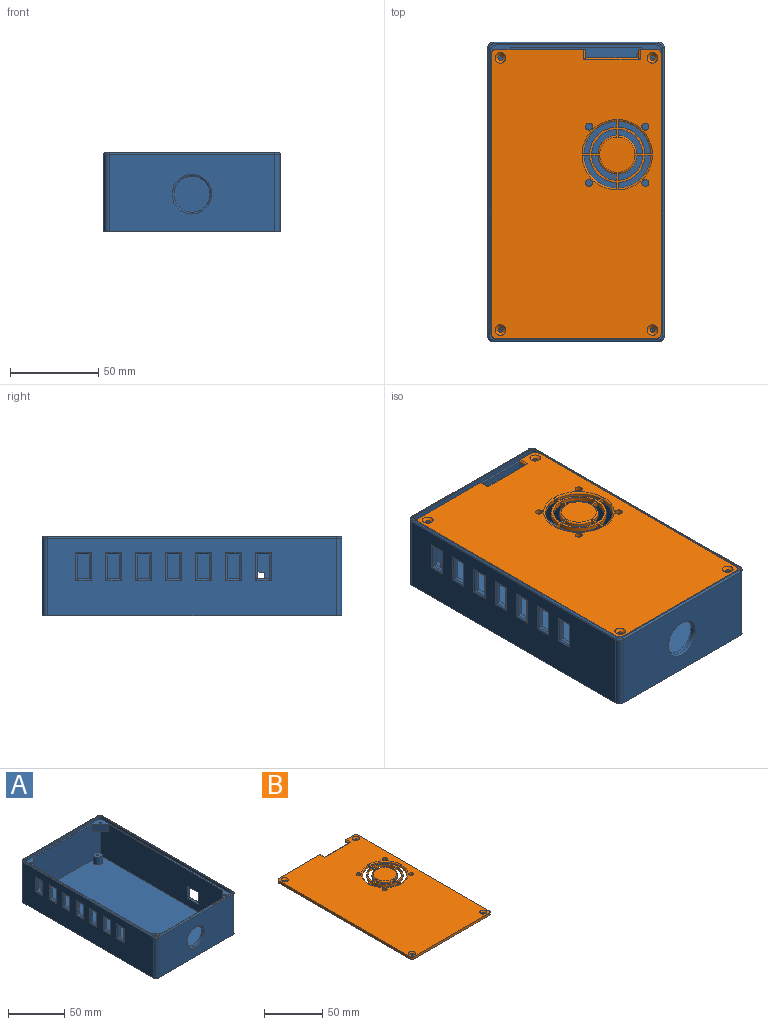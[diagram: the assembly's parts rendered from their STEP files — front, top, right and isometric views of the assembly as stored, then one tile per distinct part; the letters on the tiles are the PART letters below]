
ASSEMBLY  parts=2 mates=1
PART A: 130 faces, bbox 100.5x170.5x45 mm
  f0: plane 164x39mm, normal (-1,0,0), area 6067mm2, adj f1,f13,f14,f15,f32,f33,f34,f35
  f1: plane 94x39mm, normal (0,-1,0), area 3506mm2, adj f0,f3,f13,f14,f73,f74,f75,f76
  f2: plane 164x44mm, normal (-1,0,0), area 6208mm2, adj f8,f67,f68,f95,f98,f99,f100,f101
  f3: plane 164x39mm, normal (1,0,0), area 5550mm2, adj f1,f13,f14,f15,f36,f37,f38,f39
  f4: plane 168x98mm, normal (0,0,1), area 322.1mm2, adj f9,f10,f11,f12,f69,f70,f71,f72
  f5: plane 94x44mm, normal (0,-1,0), area 3738.4mm2, adj f8,f65,f68,f91,f97
  f6: plane 164x44mm, normal (1,0,0), area 6991mm2, adj f8,f65,f66,f90,f126,f127,f128,f129
  f7: plane 94x44mm, normal (0,1,0), area 4136mm2, adj f8,f66,f67,f94
  f8: plane 170x100mm, normal (0,0,-1), area 16992.3mm2, adj f2,f5,f6,f7,f65,f66,f67,f68
  f9: plane 90.8x3mm, normal (0,-1,0), area 272.4mm2, adj f4,f13,f69,f72
  f10: plane 160.8x3mm, normal (1,0,0), area 482.4mm2, adj f4,f13,f69,f70
  f11: plane 90.8x3mm, normal (0,1,0), area 272.4mm2, adj f4,f13,f70,f71
  f12: plane 160.8x3mm, normal (-1,0,0), area 482.4mm2, adj f4,f13,f71,f72
  f13: plane 166.8x96.8mm, normal (0,0,1), area 909.9mm2, adj f0,f1,f3,f9,f10,f11,f12,f15
  f14: plane 164x94mm, normal (0,0,1), area 15214.9mm2, adj f0,f1,f3,f15,f17,f21,f25,f29
  f15: plane 94x39mm, normal (0,1,0), area 3175.9mm2, adj f0,f3,f13,f14,f64,f77,f78,f79
  f16: cylinder r=1mm len=8mm, axis (0,0,-1), area 50.3mm2, adj f18,f19
  f17: cylinder r=4mm len=8mm, axis (0,0,-1), area 201.1mm2, adj f14,f18
  f18: plane 8x8mm, normal (0,0,1), area 47.1mm2, adj f16,f17
  f19: plane 2x2mm, normal (0,0,1), area 3.1mm2, adj f16
  f20: cylinder r=1mm len=8mm, axis (0,0,-1), area 50.3mm2, adj f22,f23
  f21: cylinder r=4mm len=8mm, axis (0,0,-1), area 201.1mm2, adj f14,f22
  f22: plane 8x8mm, normal (0,0,1), area 47.1mm2, adj f20,f21
  f23: plane 2x2mm, normal (0,0,1), area 3.1mm2, adj f20
  f24: cylinder r=1mm len=8mm, axis (0,0,-1), area 50.3mm2, adj f26,f27
  f25: cylinder r=4mm len=8mm, axis (0,0,-1), area 201.1mm2, adj f14,f26
  f26: plane 8x8mm, normal (0,0,1), area 47.1mm2, adj f24,f25
  f27: plane 2x2mm, normal (0,0,1), area 3.1mm2, adj f24
  f28: cylinder r=1mm len=8mm, axis (0,0,-1), area 50.3mm2, adj f30,f31
  f29: cylinder r=4mm len=8mm, axis (0,0,-1), area 201.1mm2, adj f14,f30
  f30: plane 8x8mm, normal (0,0,1), area 47.1mm2, adj f28,f29
  f31: plane 2x2mm, normal (0,0,1), area 3.1mm2, adj f28
  f32: plane 13x2mm, normal (0,1,0), area 26mm2, adj f0,f33,f34,f127
  f33: plane 13x2mm, normal (0,0,-1), area 26mm2, adj f0,f32,f35,f126
  f34: plane 13x2mm, normal (0,0,1), area 26mm2, adj f0,f32,f35,f129
  f35: plane 13x2mm, normal (0,-1,0), area 26mm2, adj f0,f33,f34,f128
  f36: plane 7x2mm, normal (0,0,1), area 14mm2, adj f3,f37,f39,f123
  f37: plane 14x2mm, normal (0,1,0), area 28mm2, adj f3,f36,f38,f125
  f38: plane 7x2mm, normal (0,0,-1), area 14mm2, adj f3,f37,f39,f124
  f39: plane 14x2mm, normal (0,-1,0), area 28mm2, adj f3,f36,f38,f122
  f40: plane 7x2mm, normal (0,0,1), area 14mm2, adj f3,f41,f43,f118
  f41: plane 14x2mm, normal (0,1,0), area 28mm2, adj f3,f40,f42,f119
  f42: plane 7x2mm, normal (0,0,-1), area 14mm2, adj f3,f41,f43,f121
  f43: plane 14x2mm, normal (0,-1,0), area 28mm2, adj f3,f40,f42,f120
  f44: plane 7x2mm, normal (0,0,1), area 14mm2, adj f3,f45,f47,f115
  f45: plane 14x2mm, normal (0,1,0), area 28mm2, adj f3,f44,f46,f117
  f46: plane 7x2mm, normal (0,0,-1), area 14mm2, adj f3,f45,f47,f116
  f47: plane 14x2mm, normal (0,-1,0), area 28mm2, adj f3,f44,f46,f114
  f48: plane 7x2mm, normal (0,0,1), area 14mm2, adj f3,f49,f51,f111
  f49: plane 14x2mm, normal (0,1,0), area 28mm2, adj f3,f48,f50,f113
  f50: plane 7x2mm, normal (0,0,-1), area 14mm2, adj f3,f49,f51,f112
  f51: plane 14x2mm, normal (0,-1,0), area 28mm2, adj f3,f48,f50,f110
  f52: plane 7x2mm, normal (0,0,1), area 14mm2, adj f3,f53,f55,f107
  f53: plane 14x2mm, normal (0,1,0), area 28mm2, adj f3,f52,f54,f109
  f54: plane 7x2mm, normal (0,0,-1), area 14mm2, adj f3,f53,f55,f108
  f55: plane 14x2mm, normal (0,-1,0), area 28mm2, adj f3,f52,f54,f106
  f56: plane 7x2mm, normal (0,0,1), area 14mm2, adj f3,f57,f59,f103
  f57: plane 14x2mm, normal (0,1,0), area 28mm2, adj f3,f56,f58,f105
  f58: plane 7x2mm, normal (0,0,-1), area 14mm2, adj f3,f57,f59,f104
  f59: plane 14x2mm, normal (0,-1,0), area 28mm2, adj f3,f56,f58,f102
  f60: plane 7x2mm, normal (0,0,-1), area 14mm2, adj f3,f61,f63,f99
  f61: plane 14x2mm, normal (0,-1,0), area 28mm2, adj f3,f60,f62,f101
  f62: plane 7x2mm, normal (0,0,1), area 14mm2, adj f3,f61,f63,f100
  f63: plane 14x2mm, normal (0,1,0), area 28mm2, adj f3,f60,f62,f98
  f64: cylinder r=10.25mm len=20.5mm, axis (0,-1,0), area 128.8mm2, adj f15,f97
  f65: cylinder r=3mm len=44mm, axis (0,0,1), area 207.3mm2, adj f5,f6,f8,f89
  f66: cylinder r=3mm len=44mm, axis (0,0,-1), area 207.3mm2, adj f6,f7,f8,f92
  f67: cylinder r=3mm len=44mm, axis (0,0,1), area 207.3mm2, adj f2,f7,f8,f96
  f68: cylinder r=3mm len=44mm, axis (0,0,-1), area 207.3mm2, adj f2,f5,f8,f93
  f69: cylinder r=3mm len=3mm, axis (0,0,1), area 14.1mm2, adj f4,f9,f10,f13
  f70: cylinder r=3mm len=3mm, axis (0,0,-1), area 14.1mm2, adj f4,f10,f11,f13
  f71: cylinder r=3mm len=3mm, axis (0,0,1), area 14.1mm2, adj f4,f11,f12,f13
  f72: cylinder r=3mm len=3mm, axis (0,0,-1), area 14.1mm2, adj f4,f9,f12,f13
  f73: plane 10x10mm, normal (0.71,-0.71,0), area 113.1mm2, adj f1,f3,f13,f74
  f74: plane 10x10mm, normal (0,0,-1), area 50mm2, adj f1,f3,f73
  f75: plane 10x10mm, normal (-0.71,-0.71,0), area 113.1mm2, adj f0,f1,f13,f76
  f76: plane 10x10mm, normal (0,0,-1), area 50mm2, adj f0,f1,f75
  f77: plane 10x10mm, normal (-0.71,0.71,0), area 113.1mm2, adj f0,f13,f15,f78
  f78: plane 10x10mm, normal (0,0,-1), area 50mm2, adj f0,f15,f77
  f79: plane 10x10mm, normal (0.71,0.71,0), area 113.1mm2, adj f3,f13,f15,f80
  f80: plane 10x10mm, normal (0,0,-1), area 50mm2, adj f3,f15,f79
  f81: cone r=0mm half-angle=59deg, axis (0,0,1), area 3.7mm2, adj f82
  f82: cylinder r=1mm len=6mm, axis (0,0,1), area 37.7mm2, adj f13,f81
  f83: cone r=0mm half-angle=59deg, axis (0,0,1), area 3.7mm2, adj f84
  f84: cylinder r=1mm len=6mm, axis (0,0,1), area 37.7mm2, adj f13,f83
  f85: cone r=0mm half-angle=59deg, axis (0,0,1), area 3.7mm2, adj f86
  f86: cylinder r=1mm len=6mm, axis (0,0,1), area 37.7mm2, adj f13,f85
  f87: cone r=0mm half-angle=59deg, axis (0,0,1), area 3.7mm2, adj f88
  f88: cylinder r=1mm len=6mm, axis (0,0,1), area 37.7mm2, adj f13,f87
  f89: torus R=2mm, axis (0,0,1), area 6.5mm2, adj f4,f65,f90,f91
  f90: cylinder r=1mm len=164mm, axis (0,-1,0), area 257.6mm2, adj f4,f6,f89,f92
  f91: cylinder r=1mm len=94mm, axis (-1,0,0), area 147.7mm2, adj f4,f5,f89,f93
  f92: torus R=2mm, axis (0,0,1), area 6.5mm2, adj f4,f66,f90,f94
  f93: torus R=2mm, axis (0,0,1), area 6.5mm2, adj f4,f68,f91,f95
  f94: cylinder r=1mm len=94mm, axis (1,0,0), area 147.7mm2, adj f4,f7,f92,f96
  f95: cylinder r=1mm len=164mm, axis (0,1,0), area 257.6mm2, adj f2,f4,f93,f96
  f96: torus R=2mm, axis (0,0,1), area 6.5mm2, adj f4,f67,f94,f95
  f97: torus R=11.25mm, axis (0,-1,0), area 104.7mm2, adj f5,f64
  f98: cylinder r=1mm len=16mm, axis (0,0,-1), area 23.1mm2, adj f2,f63,f99,f100
  f99: cylinder r=1mm len=9mm, axis (0,-1,0), area 12.1mm2, adj f2,f60,f98,f101
  f100: cylinder r=1mm len=9mm, axis (0,1,0), area 12.1mm2, adj f2,f62,f98,f101
  f101: cylinder r=1mm len=16mm, axis (0,0,1), area 23.1mm2, adj f2,f61,f99,f100
  f102: cylinder r=1mm len=16mm, axis (0,0,1), area 23.1mm2, adj f2,f59,f103,f104
  f103: cylinder r=1mm len=9mm, axis (0,1,0), area 12.1mm2, adj f2,f56,f102,f105
  f104: cylinder r=1mm len=9mm, axis (0,-1,0), area 12.1mm2, adj f2,f58,f102,f105
  f105: cylinder r=1mm len=16mm, axis (0,0,-1), area 23.1mm2, adj f2,f57,f103,f104
  f106: cylinder r=1mm len=16mm, axis (0,0,1), area 23.1mm2, adj f2,f55,f107,f108
  f107: cylinder r=1mm len=9mm, axis (0,1,0), area 12.1mm2, adj f2,f52,f106,f109
  f108: cylinder r=1mm len=9mm, axis (0,-1,0), area 12.1mm2, adj f2,f54,f106,f109
  f109: cylinder r=1mm len=16mm, axis (0,0,-1), area 23.1mm2, adj f2,f53,f107,f108
  f110: cylinder r=1mm len=16mm, axis (0,0,1), area 23.1mm2, adj f2,f51,f111,f112
  f111: cylinder r=1mm len=9mm, axis (0,1,0), area 12.1mm2, adj f2,f48,f110,f113
  f112: cylinder r=1mm len=9mm, axis (0,-1,0), area 12.1mm2, adj f2,f50,f110,f113
  f113: cylinder r=1mm len=16mm, axis (0,0,-1), area 23.1mm2, adj f2,f49,f111,f112
  f114: cylinder r=1mm len=16mm, axis (0,0,1), area 23.1mm2, adj f2,f47,f115,f116
  f115: cylinder r=1mm len=9mm, axis (0,1,0), area 12.1mm2, adj f2,f44,f114,f117
  f116: cylinder r=1mm len=9mm, axis (0,-1,0), area 12.1mm2, adj f2,f46,f114,f117
  f117: cylinder r=1mm len=16mm, axis (0,0,-1), area 23.1mm2, adj f2,f45,f115,f116
  f118: cylinder r=1mm len=9mm, axis (0,1,0), area 12.1mm2, adj f2,f40,f119,f120
  f119: cylinder r=1mm len=16mm, axis (0,0,-1), area 23.1mm2, adj f2,f41,f118,f121
  f120: cylinder r=1mm len=16mm, axis (0,0,1), area 23.1mm2, adj f2,f43,f118,f121
  f121: cylinder r=1mm len=9mm, axis (0,-1,0), area 12.1mm2, adj f2,f42,f119,f120
  f122: cylinder r=1mm len=16mm, axis (0,0,1), area 23.1mm2, adj f2,f39,f123,f124
  f123: cylinder r=1mm len=9mm, axis (0,1,0), area 12.1mm2, adj f2,f36,f122,f125
  f124: cylinder r=1mm len=9mm, axis (0,-1,0), area 12.1mm2, adj f2,f38,f122,f125
  f125: cylinder r=1mm len=16mm, axis (0,0,-1), area 23.1mm2, adj f2,f37,f123,f124
  f126: cylinder r=1mm len=15mm, axis (0,-1,0), area 21.6mm2, adj f6,f33,f127,f128
  f127: cylinder r=1mm len=15mm, axis (0,0,-1), area 21.6mm2, adj f6,f32,f126,f129
  f128: cylinder r=1mm len=15mm, axis (0,0,1), area 21.6mm2, adj f6,f35,f126,f129
  f129: cylinder r=1mm len=15mm, axis (0,1,0), area 21.6mm2, adj f6,f34,f127,f128
PART B: 69 faces, bbox 96.3x164.5x2.5 mm
  f0: plane 50.3x2.5mm, normal (0,1,0), area 125.5mm2, adj f1,f2,f9,f16,f68
  f1: plane 164.5x96.3mm, normal (0,0,1), area 14691.9mm2, adj f0,f3,f4,f5,f6,f7,f8,f9
  f2: plane 164.5x96.3mm, normal (0,0,-1), area 14997.6mm2, adj f0,f3,f4,f5,f6,f7,f8,f9
  f3: plane 90.3x2.5mm, normal (0,-1,0), area 225.8mm2, adj f1,f2,f7,f10
  f4: plane 158.5x2.5mm, normal (1,0,0), area 396.2mm2, adj f1,f2,f7,f8
  f5: plane 10x2.5mm, normal (0,1,0), area 24.8mm2, adj f1,f2,f8,f15,f66
  f6: plane 158.5x2.5mm, normal (-1,0,0), area 396.2mm2, adj f1,f2,f9,f10
  f7: cylinder r=3mm len=3mm, axis (0,0,1), area 11.8mm2, adj f1,f2,f3,f4
  f8: cylinder r=3mm len=3mm, axis (0,0,-1), area 11.8mm2, adj f1,f2,f4,f5
  f9: cylinder r=3mm len=3mm, axis (0,0,1), area 11.8mm2, adj f0,f1,f2,f6
  f10: cylinder r=3mm len=3mm, axis (0,0,-1), area 11.8mm2, adj f1,f2,f3,f6
  f11: plane 4.51x2.5mm, normal (0,-1,0), area 9mm2, adj f1,f2,f12,f13,f65
  f12: cylinder r=11mm len=10.38mm, axis (0,0,1), area 24.1mm2, adj f2,f11,f14,f65
  f13: cylinder r=14.5mm len=13.89mm, axis (0,0,1), area 53.9mm2, adj f1,f2,f11,f14
  f14: plane 4.51x2.5mm, normal (-1,0,0), area 9mm2, adj f1,f2,f12,f13,f65
  f15: plane 5x1.5mm, normal (-1,0,0), area 7.5mm2, adj f2,f5,f17,f66
  f16: plane 5x1.5mm, normal (1,0,0), area 7.5mm2, adj f0,f2,f17,f68
  f17: plane 30x1.5mm, normal (0,1,0), area 45mm2, adj f2,f15,f16,f67
  f18: cylinder r=19mm len=18.39mm, axis (0,0,1), area 43mm2, adj f2,f19,f20,f58
  f19: plane 4.31x2.51mm, normal (0,1,0), area 8.5mm2, adj f1,f2,f18,f21,f58
  f20: plane 4.31x2.51mm, normal (1,0,0), area 8.5mm2, adj f1,f2,f18,f21,f58
  f21: cylinder r=15.7mm len=15.09mm, axis (0,0,1), area 58.7mm2, adj f1,f2,f19,f20
  f22: cylinder r=19mm len=18.39mm, axis (0,0,1), area 43mm2, adj f2,f23,f24,f59
  f23: plane 4.31x2.51mm, normal (1,0,0), area 8.5mm2, adj f1,f2,f22,f25,f59
  f24: plane 4.31x2.51mm, normal (0,-1,0), area 8.5mm2, adj f1,f2,f22,f25,f59
  f25: cylinder r=15.7mm len=15.09mm, axis (0,0,1), area 58.7mm2, adj f1,f2,f23,f24
  f26: plane 4.31x2.51mm, normal (-1,0,0), area 8.5mm2, adj f1,f2,f27,f29,f60
  f27: cylinder r=15.7mm len=15.09mm, axis (0,0,1), area 58.7mm2, adj f1,f2,f26,f28
  f28: plane 4.31x2.51mm, normal (0,-1,0), area 8.5mm2, adj f1,f2,f27,f29,f60
  f29: cylinder r=19mm len=18.39mm, axis (0,0,1), area 43mm2, adj f2,f26,f28,f60
  f30: plane 4.51x2.5mm, normal (-1,0,0), area 9mm2, adj f1,f2,f31,f32,f62
  f31: cylinder r=11mm len=10.38mm, axis (0,0,1), area 24.1mm2, adj f2,f30,f33,f62
  f32: cylinder r=14.5mm len=13.89mm, axis (0,0,1), area 53.9mm2, adj f1,f2,f30,f33
  f33: plane 4.51x2.5mm, normal (0,1,0), area 9mm2, adj f1,f2,f31,f32,f62
  f34: cylinder r=19mm len=18.39mm, axis (0,0,1), area 43mm2, adj f2,f35,f36,f61
  f35: plane 4.31x2.51mm, normal (-1,0,0), area 8.5mm2, adj f1,f2,f34,f37,f61
  f36: plane 4.31x2.51mm, normal (0,1,0), area 8.5mm2, adj f1,f2,f34,f37,f61
  f37: cylinder r=15.7mm len=15.09mm, axis (0,0,1), area 58.7mm2, adj f1,f2,f35,f36
  f38: cylinder r=11mm len=10.38mm, axis (0,0,1), area 24.1mm2, adj f2,f39,f41,f63
  f39: plane 4.51x2.5mm, normal (0,1,0), area 9mm2, adj f1,f2,f38,f40,f63
  f40: cylinder r=14.5mm len=13.89mm, axis (0,0,1), area 53.9mm2, adj f1,f2,f39,f41
  f41: plane 4.51x2.5mm, normal (1,0,0), area 9mm2, adj f1,f2,f38,f40,f63
  f42: cylinder r=11mm len=10.38mm, axis (0,0,1), area 24.1mm2, adj f2,f43,f45,f64
  f43: plane 4.51x2.5mm, normal (1,0,0), area 9mm2, adj f1,f2,f42,f44,f64
  f44: cylinder r=14.5mm len=13.89mm, axis (0,0,1), area 53.9mm2, adj f1,f2,f43,f45
  f45: plane 4.51x2.5mm, normal (0,-1,0), area 9mm2, adj f1,f2,f42,f44,f64
  f46: cylinder r=1.5mm len=3mm, axis (0,0,1), area 9.4mm2, adj f2,f47
  f47: cone r=1.5mm half-angle=45deg, axis (0,0,1), area 30mm2, adj f1,f46
  f48: cylinder r=1.5mm len=3mm, axis (0,0,1), area 9.4mm2, adj f2,f49
  f49: cone r=1.5mm half-angle=45deg, axis (0,0,1), area 30mm2, adj f1,f48
  f50: cylinder r=1.5mm len=3mm, axis (0,0,1), area 9.4mm2, adj f2,f51
  f51: cone r=1.5mm half-angle=45deg, axis (0,0,1), area 30mm2, adj f1,f50
  f52: cylinder r=1.5mm len=3mm, axis (0,0,1), area 9.4mm2, adj f2,f53
  f53: cone r=1.5mm half-angle=45deg, axis (0,0,1), area 30mm2, adj f1,f52
  f54: cylinder r=2mm len=4mm, axis (0,0,1), area 31.4mm2, adj f1,f2
  f55: cylinder r=2mm len=4mm, axis (0,0,1), area 31.4mm2, adj f1,f2
  f56: cylinder r=2mm len=4mm, axis (0,0,1), area 31.4mm2, adj f1,f2
  f57: cylinder r=2mm len=4mm, axis (0,0,1), area 31.4mm2, adj f1,f2
  f58: torus R=20mm, axis (0,0,1), area 45.9mm2, adj f1,f18,f19,f20
  f59: torus R=20mm, axis (0,0,1), area 45.9mm2, adj f1,f22,f23,f24
  f60: torus R=20mm, axis (0,0,1), area 45.9mm2, adj f1,f26,f28,f29
  f61: torus R=20mm, axis (0,0,1), area 45.9mm2, adj f1,f34,f35,f36
  f62: torus R=10mm, axis (0,0,1), area 24.4mm2, adj f1,f30,f31,f33
  f63: torus R=10mm, axis (0,0,1), area 24.4mm2, adj f1,f38,f39,f41
  f64: torus R=10mm, axis (0,0,1), area 24.4mm2, adj f1,f42,f43,f45
  f65: torus R=10mm, axis (0,0,1), area 24.4mm2, adj f1,f11,f12,f14
  f66: cylinder r=1mm len=6mm, axis (0,-1,0), area 8.4mm2, adj f1,f5,f15,f67
  f67: cylinder r=1mm len=32mm, axis (-1,0,0), area 48.3mm2, adj f1,f17,f66,f68
  f68: cylinder r=1mm len=6mm, axis (0,1,0), area 8.4mm2, adj f0,f1,f16,f67
PLACE A t=(-132.77,-22.76,69.45)mm
PLACE B t=(-132.52,-23.91,111.45)mm
MATE fastened B.f48 <-> A.f85  axis (0,0,-1) through (-89.37,-101.16,111.45)mm
